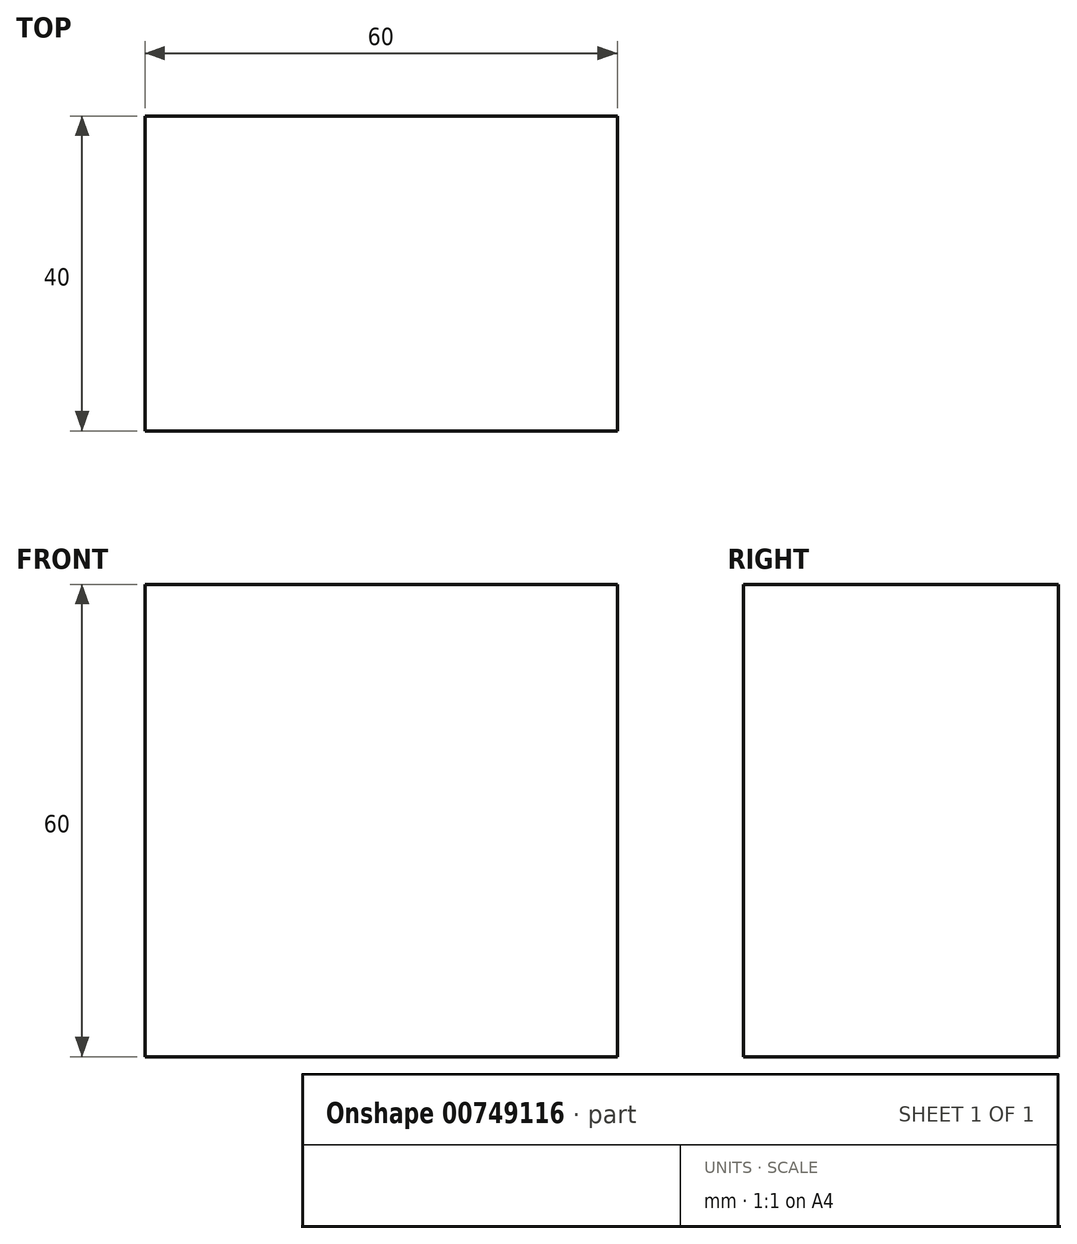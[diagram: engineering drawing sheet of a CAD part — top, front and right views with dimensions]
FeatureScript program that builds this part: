
annotation { "Feature Type Name" : "Feature", "Feature Type Description" : "" }
export const myFeature = defineFeature(function(context is Context, id is Id, definition is map)
    precondition{}
    {
        {
            var Q0;
            Q0=qCreatedBy(makeId("Front.planeOp"),FACE);
            var sketch = newSketch(context, id + "F0", { "sketchPlane" : qUnion([Q0])});
            skLineSegment(sketch, "E0.bottom", {"start": v(-30, -30) * mm, "end": v(30, -30) * mm});
            skLineSegment(sketch, "E0.top", {"start": v(-30, 30) * mm, "end": v(30, 30) * mm});
            skLineSegment(sketch, "E0.left", {"start": v(-30, -30) * mm, "end": v(-30, 30) * mm});
            skLineSegment(sketch, "E0.right", {"start": v(30, -30) * mm, "end": v(30, 30) * mm});
            skPoint(sketch, "E0.middle", {"position": v(0, 0) * mm});
            skSolve(sketch);
        }
        {
            var Q0;
            Q0=makeQuery(id+"F0.imprint","IMPRINT",FACE,{"disambiguationData":[TD([[makeQuery(id+"F0.imprint","IMPRINT",EDGE,{"derivedFrom":sQuery(id+"F0.wireOp",EDGE,"E0.bottom")}),1.0]])]});
            extrude(context, id + "F1", {"entities" : qUnion([Q0]), "depth" : 40 * mm, "offsetDistance" : 25 * mm});
        }
    });
